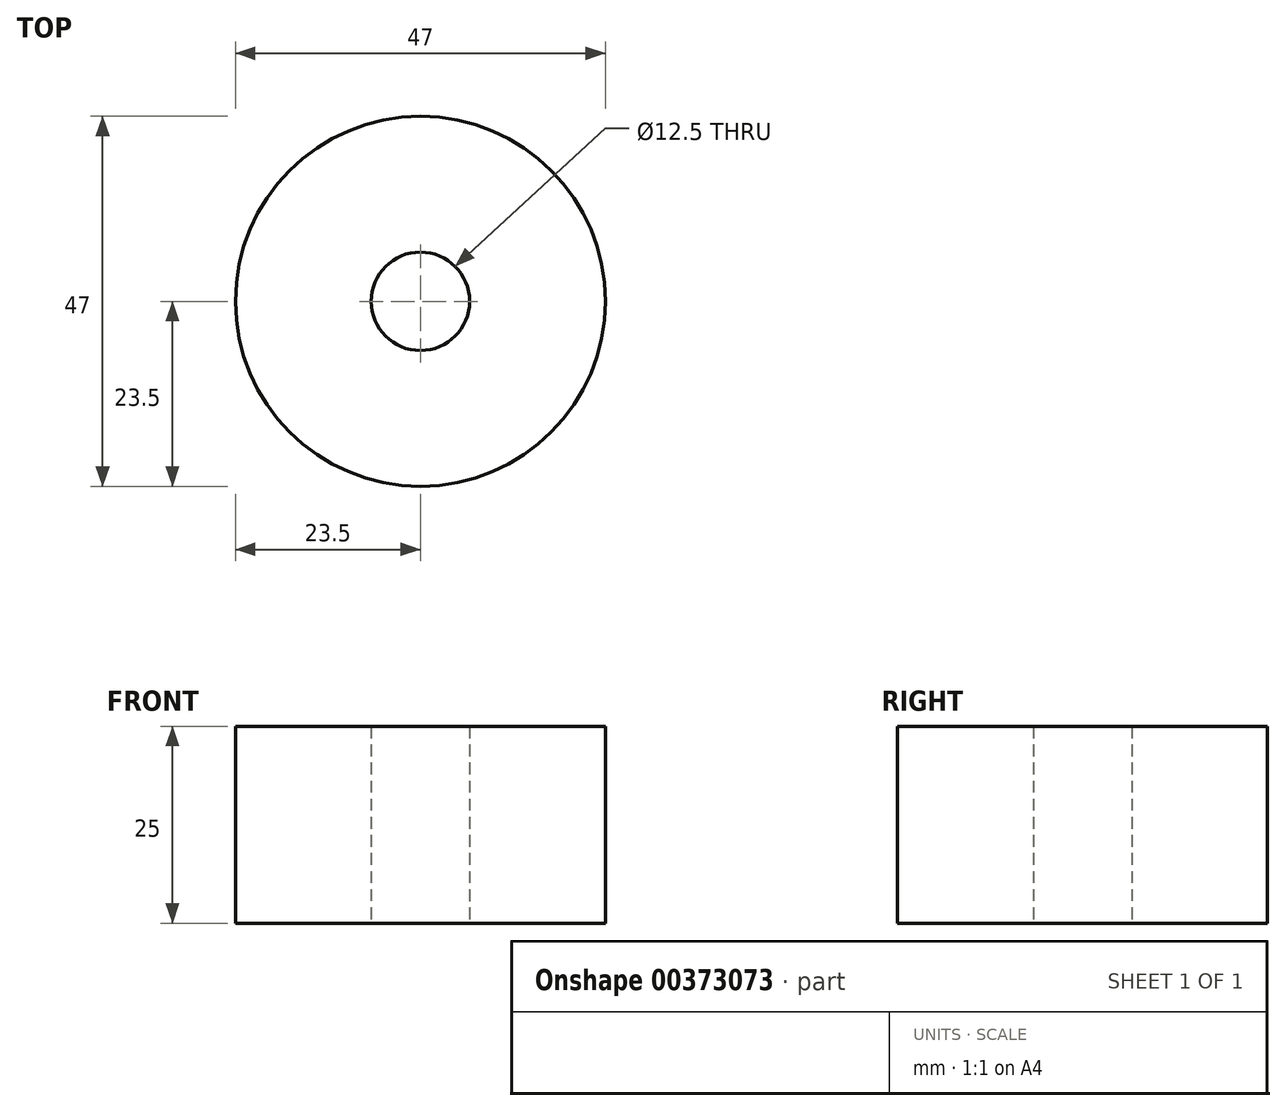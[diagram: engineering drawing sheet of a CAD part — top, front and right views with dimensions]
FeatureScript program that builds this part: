
annotation { "Feature Type Name" : "Feature", "Feature Type Description" : "" }
export const myFeature = defineFeature(function(context is Context, id is Id, definition is map)
    precondition{}
    {
        {
            var Q0;
            Q0=qCreatedBy(makeId("Top.planeOp"),FACE);
            var sketch = newSketch(context, id + "F0", { "sketchPlane" : qUnion([Q0])});
            skCircle(sketch, "E0", {"center": v(0, 0) * mm, "radius": 17.5 * mm});
            skCircle(sketch, "E1", {"center": v(0, 0) * mm, "radius": 23.5 * mm});
            skCircle(sketch, "E2", {"center": v(0, 0) * mm, "radius": 6.25 * mm});
            skSolve(sketch);
        }
        {
            var Q0;
            Q0=makeQuery(id+"F0.imprint","IMPRINT",FACE,{"disambiguationData":[TD([[makeQuery(id+"F0.imprint","IMPRINT",EDGE,{"derivedFrom":sQuery(id+"F0.wireOp",EDGE,"E0")}),-1.0]])]});
            var Q1;
            Q1=makeQuery(id+"F0.imprint","IMPRINT",FACE,{"disambiguationData":[TD([[makeQuery(id+"F0.imprint","IMPRINT",EDGE,{"derivedFrom":sQuery(id+"F0.wireOp",EDGE,"E0")}),1.0]])]});
            extrude(context, id + "F1", {"entities" : qUnion([Q0, Q1]), "depth" : 25 * mm});
        }
    });
